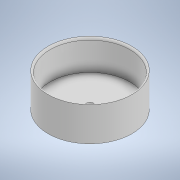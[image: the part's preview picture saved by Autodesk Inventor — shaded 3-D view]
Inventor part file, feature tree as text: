
AUTODESK INVENTOR PART (.ipt)
format: ipt  version: 2020.3 (Build 243373000, 373)  size: 130,560 bytes
history: native  units: mm
features: extrude x5, sketch x5, fillet x1
ambient origin geometry x8: Origin, YZ Plane, XZ Plane, XY Plane, X Axis, Y Axis, Z Axis, Center Point
bodies: Solid1 (feature_tree)
feature tree (11):
  extrude  "Extrusion1"  Depth=40.0mm TaperAngle=0.0deg
  extrude  "Extrusion2"  Depth=2.0mm TaperAngle=0.0deg
  extrude  "Extrusion3"  Depth=10.0mm TaperAngle=0.0deg
  extrude  "Extrusion4"  Depth=2.5mm
  extrude  "Extrusion5"  [1 undecoded]
  fillet  "Fillet1"  [1 undecoded]
  sketch  "Sketch1"  dims[d1=5.0mm d2=0.0mm d4=40.0mm d5=0.0mm]
  sketch  "Sketch2"  dims[d7=8.5mm d8=2.0mm d9=0.0mm]
  sketch  "Sketch3"  dims[d10=5.0mm d11=10.0mm d12=0.0mm]
  sketch  "Sketch4"  dims[d13=30.0mm d14=0.0mm d15=2.5mm]
  sketch  "Sketch5"
note: 2 required parameter values undecoded (feature->parameter linkage not recoverable at this tier; creation-order binding heuristic only, values carry confidence <= 0.55)
